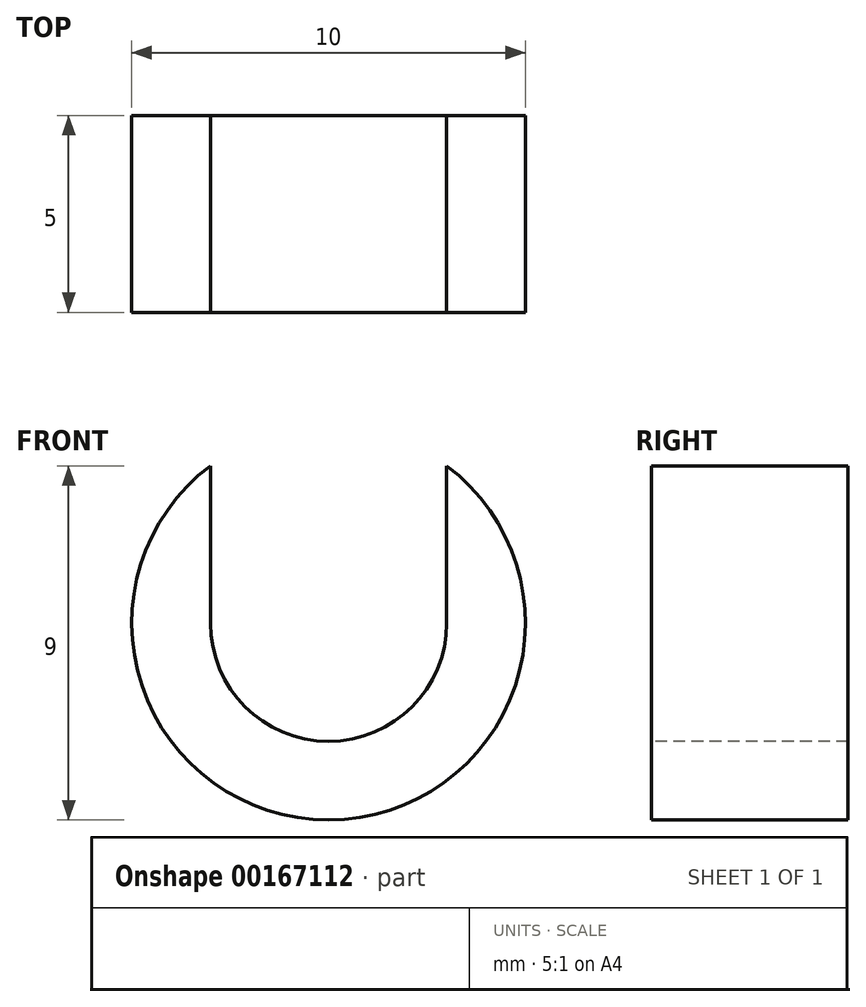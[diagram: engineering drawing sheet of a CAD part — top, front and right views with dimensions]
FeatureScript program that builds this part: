
annotation { "Feature Type Name" : "Feature", "Feature Type Description" : "" }
export const myFeature = defineFeature(function(context is Context, id is Id, definition is map)
    precondition{}
    {
        {
            var Q0;
            Q0=qCreatedBy(makeId("Front.planeOp"),FACE);
            var sketch = newSketch(context, id + "F0", { "sketchPlane" : qUnion([Q0])});
            skCircle(sketch, "E0", {"center": v(0, 0) * mm, "radius": 5 * mm});
            skSolve(sketch);
        }
        {
            var Q0;
            Q0=makeQuery(id+"F0.imprint","IMPRINT",FACE,{"disambiguationData":[TD([[makeQuery(id+"F0.imprint","IMPRINT",EDGE,{"derivedFrom":sQuery(id+"F0.wireOp",EDGE,"E0")}),1.0]])]});
            extrude(context, id + "F1", {"entities" : qUnion([Q0]), "depth" : 5 * mm});
        }
        {
            var Q0;
            Q0=makeQuery(id+"F1.opExtrude","CAP_FACE",FACE,{"disambiguationData":[OSD([sQuery(id+"F0.wireOp",EDGE,"E0")])],"isStart":false});
            var sketch = newSketch(context, id + "F2", { "sketchPlane" : qUnion([Q0])});
            skLineSegment(sketch, "E1.0", {"start": v(3, 0) * mm, "end": v(3, 4) * mm});
            skLineSegment(sketch, "E2.0", {"start": v(-3, 0) * mm, "end": v(-3, 4) * mm});
            skArc(sketch, "E3", {"start": v(3, 4) * mm, "mid": v(0, 5) * mm, "end": v(-3, 4) * mm});
            skLineSegment(sketch, "E4", {"start": v(-3, 0) * mm, "end": v(3, 0) * mm});
            skArc(sketch, "E5", {"start": v(-3, 0) * mm, "mid": v(0, -3) * mm, "end": v(3, 0) * mm});
            skSolve(sketch);
        }
        {
            var Q0;
            Q0 = qSketchRegion(id + "F2", true);
            extrude(context, id + "F3", {"entities" : qUnion([Q0]), "operationType" : NewBodyOperationType.REMOVE, "endBound" : BoundingType.THROUGH_ALL, "oppositeDirection" : true, "depth" : 25 * mm});
        }
    });
